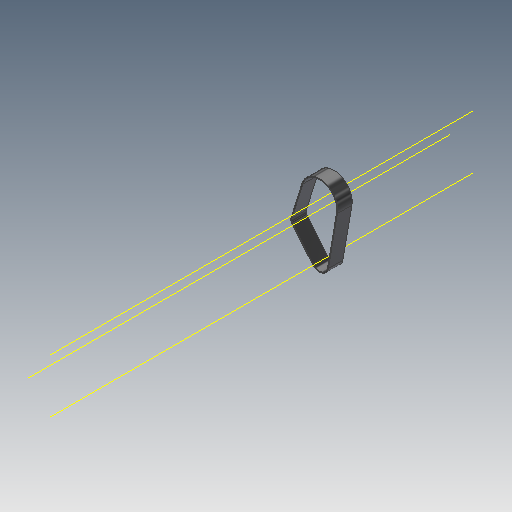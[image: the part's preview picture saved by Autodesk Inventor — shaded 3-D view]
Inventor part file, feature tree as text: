
AUTODESK INVENTOR PART (.ipt)
format: ipt  version: 2018 (Build 220112000, 112)  size: 108,032 bytes
history: native  units: mm (DEFAULTED — no unit token found)
features: other x5, plane x3, sketch x1, sweep x1
ambient origin geometry x8: Origin, YZ Plane, XZ Plane, XY Plane, X Axis, Y Axis, Z Axis, Center Point
bodies: Solid1 (feature_tree)
feature tree (10):
  sketch  "Sketch Path"  dims[d0=10.0mm d2=0.0mm d4=0.3mm d5=0.3mm d6=0.0mm d7=0.0mm d8=0.0mm d9=0.0mm d10=0.0mm d11=0.0mm d12=0.0mm d13=0.0mm]
  other  "Cross Section Plane"
  other  "Work Axis1"
  other  "Work Axis2"
  other  "Work Axis3"
  plane  "Work Plane2"
  plane  "Work Plane3"
  plane  "Work Plane4"
  sweep  "Belt"
  other  "Cross Section"
